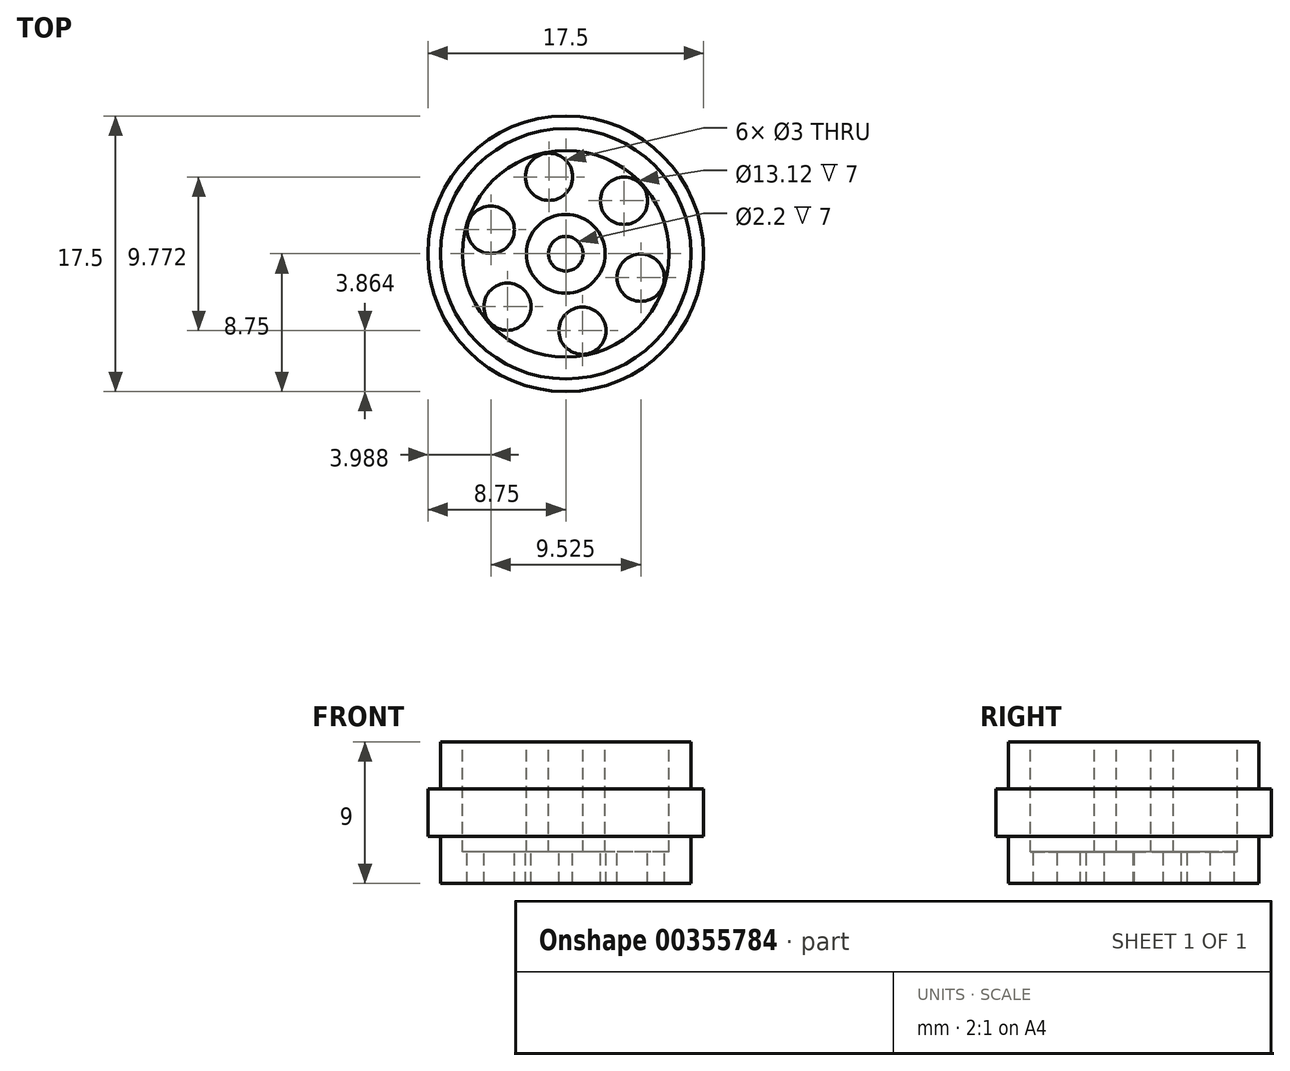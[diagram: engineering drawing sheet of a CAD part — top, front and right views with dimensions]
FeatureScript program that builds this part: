
annotation { "Feature Type Name" : "Feature", "Feature Type Description" : "" }
export const myFeature = defineFeature(function(context is Context, id is Id, definition is map)
    precondition{}
    {
        {
            var Q0;
            Q0=qCreatedBy(makeId("Top.planeOp"),FACE);
            var sketch = newSketch(context, id + "F0", { "sketchPlane" : qUnion([Q0])});
            skCircle(sketch, "E0", {"center": v(0, 0) * mm, "radius": 7.95 * mm});
            skSolve(sketch);
        }
        {
            var Q0;
            Q0 = qSketchRegion(id + "F0", true);
            extrude(context, id + "F1", {"entities" : qUnion([Q0]), "depth" : 3 * mm});
        }
        {
            var Q0;
            Q0=makeQuery(id+"F1.opExtrude","CAP_FACE",FACE,{"disambiguationData":[OSD([sQuery(id+"F0.wireOp",EDGE,"E0")])],"isStart":false});
            var sketch = newSketch(context, id + "F2", { "sketchPlane" : qUnion([Q0])});
            skCircle(sketch, "E1", {"center": v(0, 0) * mm, "radius": 8.75 * mm});
            skSolve(sketch);
        }
        {
            var Q0;
            Q0 = qSketchRegion(id + "F2", true);
            extrude(context, id + "F3", {"entities" : qUnion([Q0]), "operationType" : NewBodyOperationType.ADD, "depth" : 3 * mm});
        }
        {
            var Q0;
            Q0=makeQuery(id+"F3.opExtrude","CAP_FACE",FACE,{"disambiguationData":[OSD([sQuery(id+"F2.wireOp",EDGE,"E1")])],"isStart":false});
            var sketch = newSketch(context, id + "F4", { "sketchPlane" : qUnion([Q0])});
            skCircle(sketch, "E2", {"center": v(0, 0) * mm, "radius": 7.95 * mm});
            skSolve(sketch);
        }
        {
            var Q0;
            Q0 = qSketchRegion(id + "F4", true);
            extrude(context, id + "F5", {"entities" : qUnion([Q0]), "operationType" : NewBodyOperationType.ADD, "depth" : 3 * mm});
        }
        {
            var Q0;
            Q0=makeQuery(id+"F5.opExtrude","CAP_FACE",FACE,{"disambiguationData":[OSD([sQuery(id+"F4.wireOp",EDGE,"E2")])],"isStart":false});
            var sketch = newSketch(context, id + "F6", { "sketchPlane" : qUnion([Q0])});
            skCircle(sketch, "E3", {"center": v(0, 0) * mm, "radius": 5 * mm, "construction": true});
            skCircle(sketch, "E4", {"center": v(3.7, 3.36) * mm, "radius": 1.5 * mm});
            skCircle(sketch, "E5.1.0", {"center": v(-1.06, 4.89) * mm, "radius": 1.5 * mm});
            skCircle(sketch, "E5.2.0", {"center": v(-4.76, 1.52) * mm, "radius": 1.5 * mm});
            skCircle(sketch, "E5.3.0", {"center": v(-3.7, -3.36) * mm, "radius": 1.5 * mm});
            skCircle(sketch, "E5.4.0", {"center": v(1.06, -4.89) * mm, "radius": 1.5 * mm});
            skCircle(sketch, "E5.5.0", {"center": v(4.76, -1.52) * mm, "radius": 1.5 * mm});
            skSolve(sketch);
        }
        {
            var Q0;
            Q0 = qSketchRegion(id + "F6", true);
            extrude(context, id + "F7", {"entities" : qUnion([Q0]), "operationType" : NewBodyOperationType.REMOVE, "oppositeDirection" : true, "depth" : 25 * mm});
        }
        {
            var Q0;
            Q0=makeQuery(id+"F5.opExtrude","CAP_FACE",FACE,{"disambiguationData":[OSD([sQuery(id+"F4.wireOp",EDGE,"E2")])],"isStart":false});
            var sketch = newSketch(context, id + "F8", { "sketchPlane" : qUnion([Q0])});
            skCircle(sketch, "E6", {"center": v(0, 0) * mm, "radius": 1.1 * mm});
            skCircle(sketch, "E7", {"center": v(0, 0) * mm, "radius": 2.5 * mm});
            skCircle(sketch, "E8", {"center": v(0, 0) * mm, "radius": 6.56 * mm});
            skSolve(sketch);
        }
        {
            var Q0;
            Q0 = qSketchRegion(id + "F8", true);
            var Q1;
            Q1=makeQuery(id+"F8.imprint","IMPRINT",FACE,{"disambiguationData":[TD([[makeQuery(id+"F8.imprint","IMPRINT",EDGE,{"derivedFrom":sQuery(id+"F8.wireOp",EDGE,"E6")}),1.0]])]});
            extrude(context, id + "F9", {"entities" : qUnion([Q0, Q1]), "operationType" : NewBodyOperationType.REMOVE, "oppositeDirection" : true, "depth" : 7 * mm});
        }
    });
